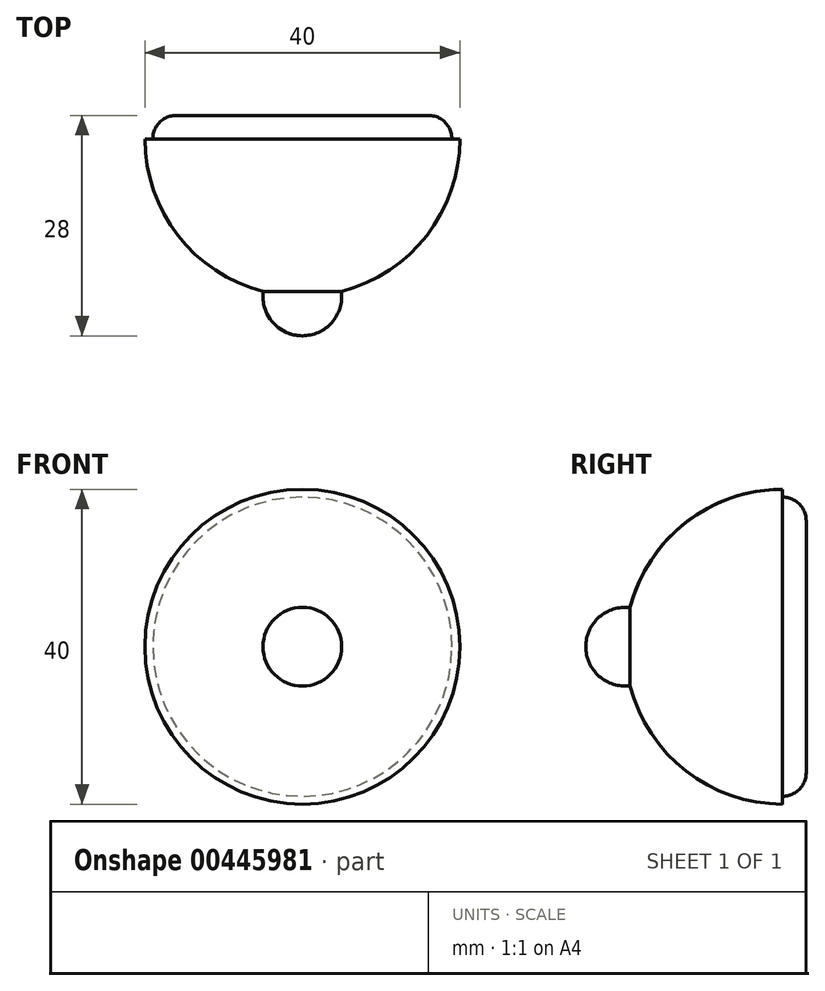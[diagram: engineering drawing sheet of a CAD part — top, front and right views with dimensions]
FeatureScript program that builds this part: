
annotation { "Feature Type Name" : "Feature", "Feature Type Description" : "" }
export const myFeature = defineFeature(function(context is Context, id is Id, definition is map)
    precondition{}
    {
        {
            var Q0;
            Q0=qCreatedBy(makeId("Top.planeOp"),FACE);
            var sketch = newSketch(context, id + "F0", { "sketchPlane" : qUnion([Q0])});
            skArc(sketch, "E0", {"start": v(-20, 0) * mm, "mid": v(-15.8, -12.26) * mm, "end": v(-4.96, -19.38) * mm});
            skLineSegment(sketch, "E1", {"start": v(0, 0) * mm, "end": v(0, -20) * mm});
            skLineSegment(sketch, "E2", {"start": v(0, 0) * mm, "end": v(-20, 0) * mm});
            skArc(sketch, "E3", {"start": v(-4.96, -19.38) * mm, "mid": v(-3.75, -23.3) * mm, "end": v(0, -25) * mm});
            skLineSegment(sketch, "E4", {"start": v(0, -20) * mm, "end": v(0, -25) * mm});
            skSolve(sketch);
        }
        {
            var Q0;
            Q0=makeQuery(id+"F0.imprint","IMPRINT",FACE,{"disambiguationData":[TD([[makeQuery(id+"F0.imprint","IMPRINT",EDGE,{"derivedFrom":sQuery(id+"F0.wireOp",EDGE,"E0")}),1.0]])]});
            var Q1;
            Q1=sQuery(id+"F0.wireOp",EDGE,"E1");
            revolve(context, id + "F1", {"entities" : qUnion([Q0]), "axis" : qUnion([Q1]), "revolveType" : RevolveType.FULL});
        }
        {
            var Q0;
            Q0=qCreatedBy(makeId("Front.planeOp"),FACE);
            var sketch = newSketch(context, id + "F2", { "sketchPlane" : qUnion([Q0])});
            skCircle(sketch, "E5", {"center": v(0, 0) * mm, "radius": 19 * mm});
            skSolve(sketch);
        }
        {
            var Q0;
            Q0=makeQuery(id+"F2.imprint","IMPRINT",FACE,{"disambiguationData":[TD([[makeQuery(id+"F2.imprint","IMPRINT",EDGE,{"derivedFrom":sQuery(id+"F2.wireOp",EDGE,"E5")}),1.0]])]});
            extrude(context, id + "F3", {"entities" : qUnion([Q0]), "operationType" : NewBodyOperationType.ADD, "oppositeDirection" : true, "depth" : 3 * mm});
        }
        {
            var Q0;
            Q0=makeQuery(id+"F3.opExtrude","CAP_EDGE",EDGE,{"disambiguationData":[OSD([sQuery(id+"F2.wireOp",EDGE,"E5")])],"isStart":false});
            fillet(context, id + "F4", {"entities" : qUnion([Q0]), "radius" : 3 * mm, "allowEdgeOverflow" : false});
        }
    });
